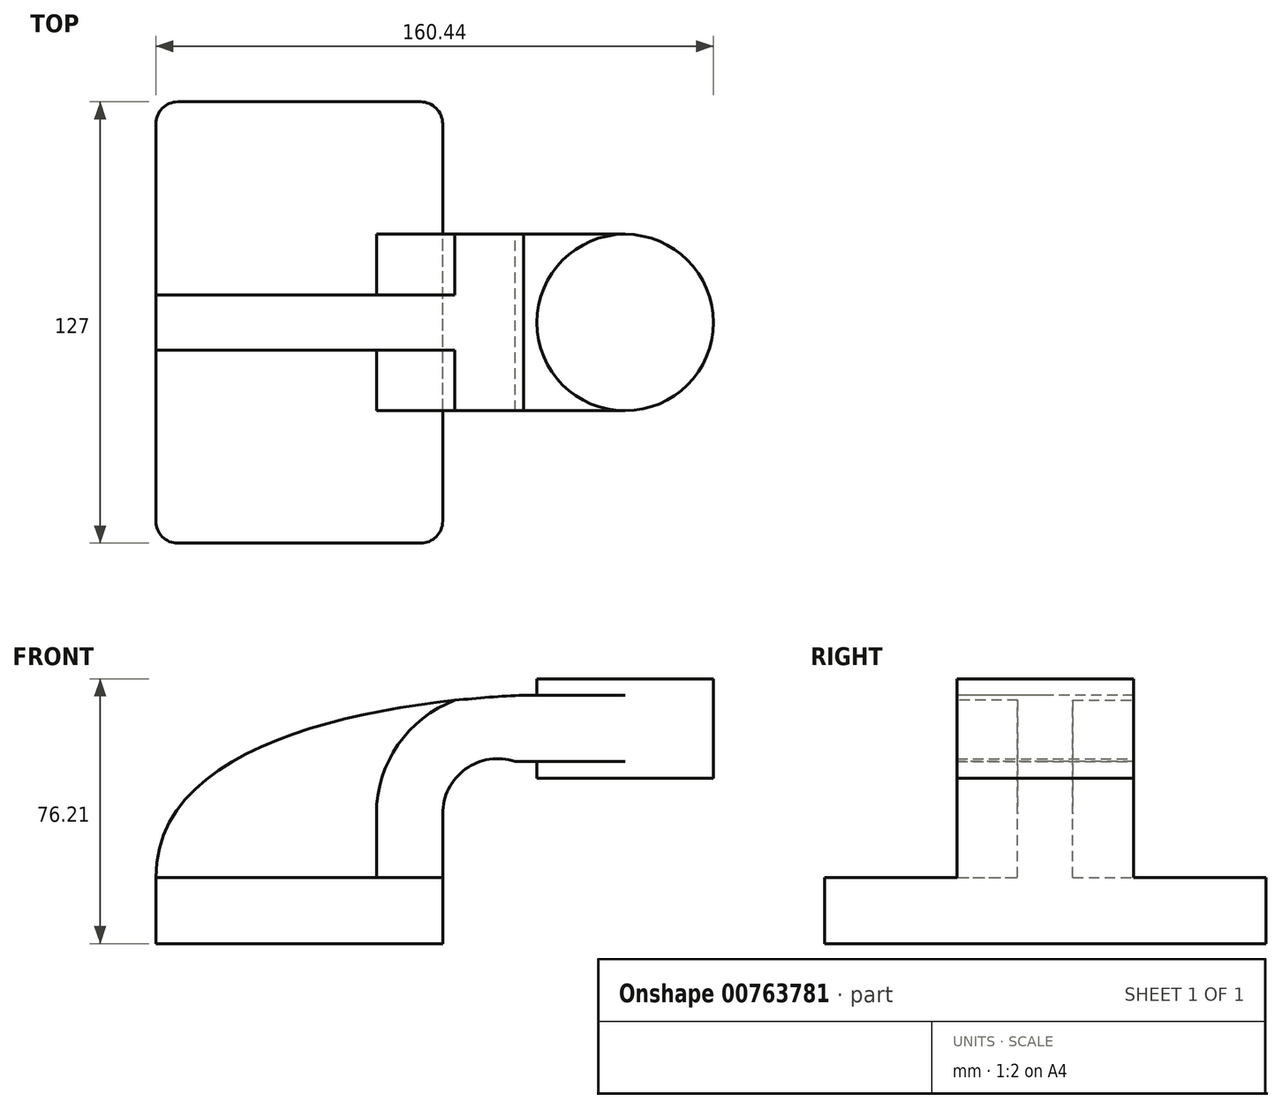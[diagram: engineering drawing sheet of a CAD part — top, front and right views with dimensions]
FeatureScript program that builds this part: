
annotation { "Feature Type Name" : "Feature", "Feature Type Description" : "" }
export const myFeature = defineFeature(function(context is Context, id is Id, definition is map)
    precondition{}
    {
        {
            var Q0;
            Q0=qCreatedBy(makeId("Front.planeOp"),FACE);
            var sketch = newSketch(context, id + "F0", { "sketchPlane" : qUnion([Q0])});
            skLineSegment(sketch, "E0.bottom", {"start": v(-41.28, 9.52) * mm, "end": v(41.27, 9.53) * mm});
            skLineSegment(sketch, "E0.top", {"start": v(-41.28, -9.53) * mm, "end": v(41.28, -9.53) * mm});
            skLineSegment(sketch, "E0.left", {"start": v(-41.28, 9.52) * mm, "end": v(-41.28, -9.53) * mm});
            skLineSegment(sketch, "E0.right", {"start": v(41.27, 9.53) * mm, "end": v(41.28, -9.52) * mm});
            skPoint(sketch, "E0.middle", {"position": v(0, 0) * mm});
            skLineSegment(sketch, "E1.bottom", {"start": v(68.36, 38.1) * mm, "end": v(119.16, 38.1) * mm});
            skLineSegment(sketch, "E1.top", {"start": v(68.36, 66.68) * mm, "end": v(119.16, 66.68) * mm});
            skLineSegment(sketch, "E1.left", {"start": v(68.36, 38.1) * mm, "end": v(68.36, 66.68) * mm});
            skLineSegment(sketch, "E1.right", {"start": v(119.16, 38.1) * mm, "end": v(119.16, 66.68) * mm});
            skPoint(sketch, "E1.middle", {"position": v(93.76, 52.39) * mm});
            skLineSegment(sketch, "E2", {"start": v(41.27, 9.53) * mm, "end": v(41.27, 27.8) * mm});
            skArc(sketch, "E3", {"start": v(41.27, 27.8) * mm, "mid": v(47.85, 40.66) * mm, "end": v(62.12, 42.88) * mm});
            skLineSegment(sketch, "E4", {"start": v(62.12, 42.88) * mm, "end": v(93.76, 42.88) * mm});
            skLineSegment(sketch, "E5.0", {"start": v(64.57, 61.93) * mm, "end": v(93.76, 61.93) * mm});
            skArc(sketch, "E5.1", {"start": v(22.22, 27.8) * mm, "mid": v(35.23, 54.99) * mm, "end": v(64.57, 61.93) * mm});
            skLineSegment(sketch, "E5.2", {"start": v(22.22, 9.53) * mm, "end": v(22.22, 27.8) * mm});
            skLineSegment(sketch, "E6", {"start": v(93.76, 38.1) * mm, "end": v(93.76, 66.68) * mm});
            skFitSpline(sketch, "E7", {"points": [v(-41.28, 9.53) * mm, v(64.57, 61.93) * mm], "startDerivative": vector(-0.2, 118.72) * mm, "endDerivative": vector(126.81, 5.44) * mm});
            skSolve(sketch);
        }
        {
            var Q0;
            Q0=makeQuery(id+"F0.imprint","IMPRINT",FACE,{"disambiguationData":[TD([[makeQuery(id+"F0.imprint","IMPRINT",EDGE,{"derivedFrom":sQuery(id+"F0.wireOp",EDGE,"E0.top")}),1.0]])]});
            extrude(context, id + "F1", {"entities" : qUnion([Q0]), "endBound" : BoundingType.SYMMETRIC, "depth" : 127 * mm, "offsetDistance" : 25.4 * mm});
        }
        {
            var Q0;
            {var subQ1=sQuery(id+"F0.wireOp",EDGE,"E2");Q0=makeQuery(id+"F0.imprint","IMPRINT",FACE,{"disambiguationData":[TD([[makeQuery(id+"F0.imprint","IMPRINT",EDGE,{"derivedFrom":subQ1}),1.0]])]});}
            var Q1;
            {var subQ0=sQuery(id+"F0.wireOp",EDGE,"E4");var subQ1=sQuery(id+"F0.wireOp",EDGE,"E1.left");var subQ2=makeQuery(id+"F0.imprint","INTERSECT",VERTEX,{"derivedFrom":[subQ1,subQ0]});Q1=makeQuery(id+"F0.imprint","IMPRINT",FACE,{"disambiguationData":[TD([[makeQuery(id+"F0.imprint","IMPRINT",EDGE,{"disambiguationData":[TD([[subQ2,-1.0]])],"derivedFrom":subQ1}),-1.0]])]});}
            extrude(context, id + "F2", {"entities" : qUnion([Q0, Q1]), "operationType" : NewBodyOperationType.ADD, "endBound" : BoundingType.SYMMETRIC, "depth" : 50.8 * mm, "offsetDistance" : 25.4 * mm});
        }
        {
            var Q0;
            {var subQ3=sQuery(id+"F0.wireOp",EDGE,"E5.2");Q0=makeQuery(id+"F0.imprint","IMPRINT",FACE,{"disambiguationData":[TD([[makeQuery(id+"F0.imprint","IMPRINT",EDGE,{"derivedFrom":subQ3}),1.0]])]});}
            extrude(context, id + "F3", {"entities" : qUnion([Q0]), "operationType" : NewBodyOperationType.ADD, "endBound" : BoundingType.SYMMETRIC, "depth" : 15.88 * mm, "offsetDistance" : 25.4 * mm});
        }
        {
            var Q0;
            {var subQ4=sQuery(id+"F0.wireOp",EDGE,"E1.right");Q0=makeQuery(id+"F0.imprint","IMPRINT",FACE,{"disambiguationData":[TD([[makeQuery(id+"F0.imprint","IMPRINT",EDGE,{"derivedFrom":subQ4}),1.0]])]});}
            var Q1;
            Q1=sQuery(id+"F0.wireOp",EDGE,"E6");
            revolve(context, id + "F4", {"operationType" : NewBodyOperationType.ADD, "surfaceOperationType" : NewSurfaceOperationType.NEW, "entities" : qUnion([Q0]), "axis" : qUnion([Q1]), "revolveType" : RevolveType.FULL});
        }
        {
            var Q0;
            Q0=makeQuery(id+"F1.opExtrude","CAP_EDGE",EDGE,{"disambiguationData":[OSD([sQuery(id+"F0.wireOp",EDGE,"E0.right")])],"isStart":false});
            var Q1;
            Q1=makeQuery(id+"F1.opExtrude","CAP_EDGE",EDGE,{"disambiguationData":[OSD([sQuery(id+"F0.wireOp",EDGE,"E0.left")])],"isStart":false});
            var Q2;
            Q2=makeQuery(id+"F1.opExtrude","CAP_EDGE",EDGE,{"disambiguationData":[OSD([sQuery(id+"F0.wireOp",EDGE,"E0.right")])],"isStart":true});
            var Q3;
            Q3=makeQuery(id+"F1.opExtrude","CAP_EDGE",EDGE,{"disambiguationData":[OSD([sQuery(id+"F0.wireOp",EDGE,"E0.left")])],"isStart":true});
            fillet(context, id + "F5", {"entities" : qUnion([Q0, Q1, Q2, Q3]), "radius" : 6.35 * mm, "tangentPropagation" : true, "allowEdgeOverflow" : false});
        }
    });
